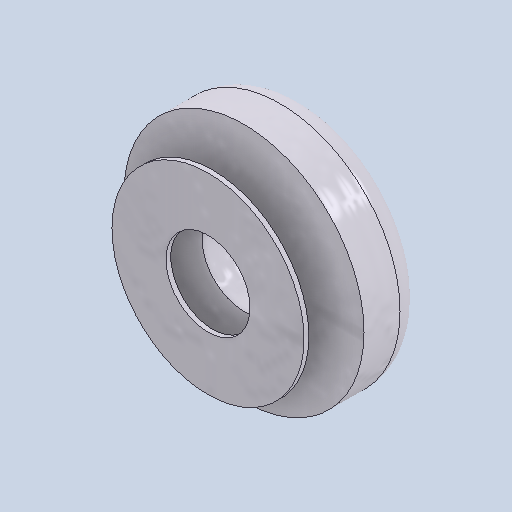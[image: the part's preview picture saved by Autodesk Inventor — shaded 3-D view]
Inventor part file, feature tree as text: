
AUTODESK INVENTOR PART (.ipt)
format: ipt  version: 2024.3 (Build 283343000, 343)  size: 298,496 bytes
history: native  units: mm
features: extrude x2, sketch x2, plane x1, fillet x1
ambient origin geometry x8: Origin, YZ Plane, XZ Plane, XY Plane, X Axis, Y Axis, Z Axis, Center Point
bodies: Solid1 (feature_tree)
feature tree (6):
  extrude  "Extrusion1"  Depth=10.0mm
  plane  "Work Plane1"
  extrude  "Extrusion2"  Depth=4.0mm
  fillet  "Fillet1"  Radius=8.0mm
  sketch  "Sketch1"  dims[d0=10.0mm d1=3.5mm]
  sketch  "Sketch2"  dims[d2=2.5mm d3=0.0mm d4=4.0mm d5=8.0mm d6=0.2mm d7=0.0mm d8=1.0mm]
